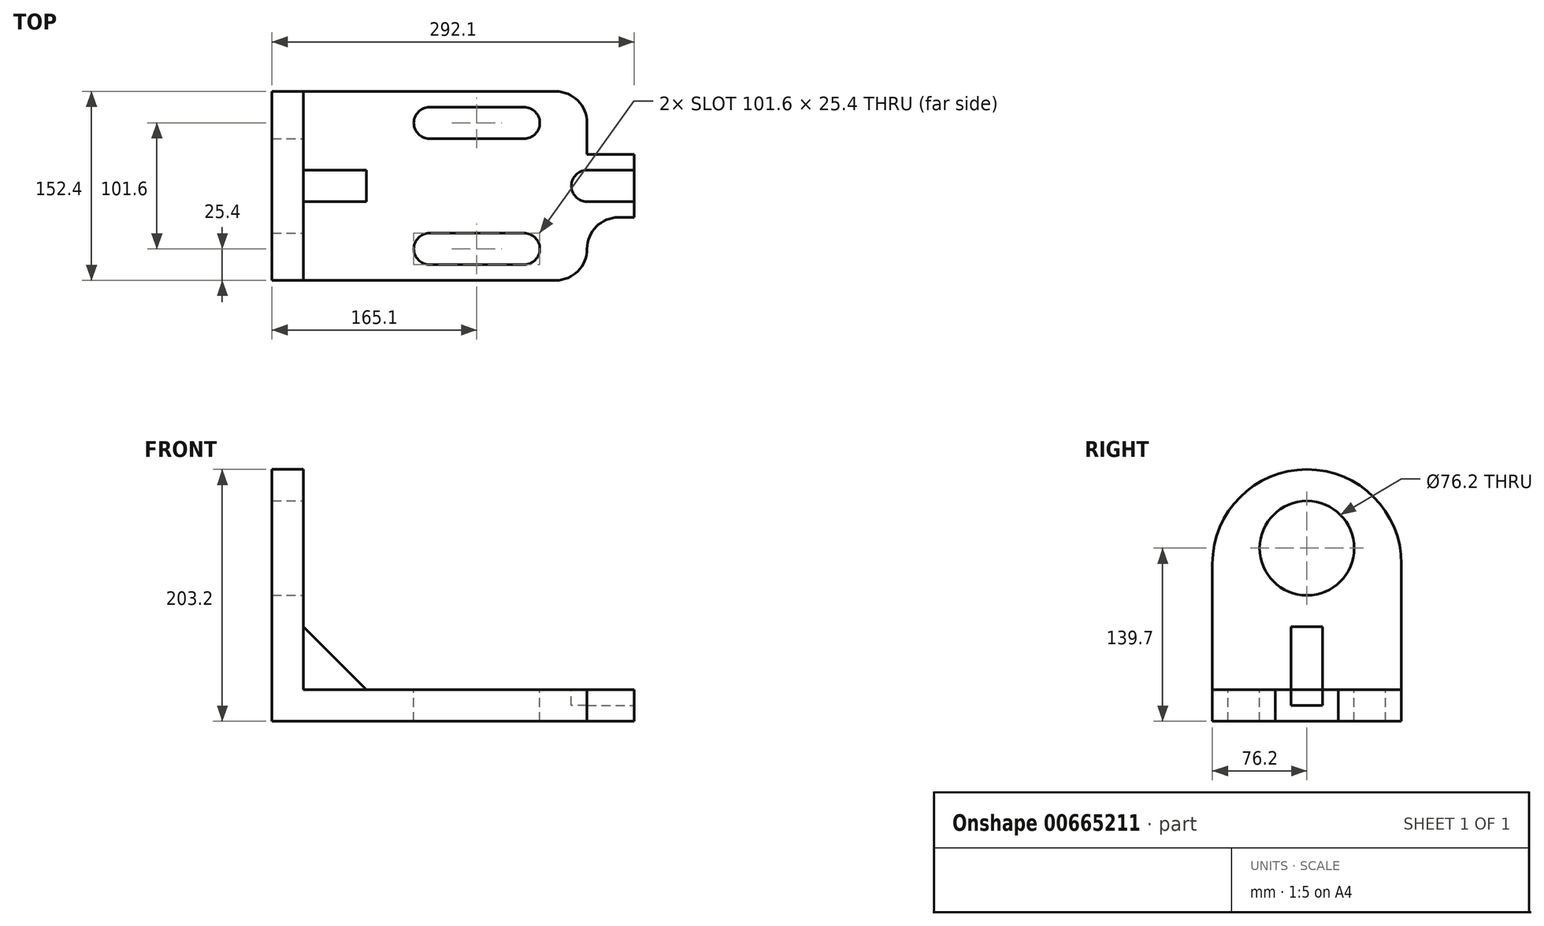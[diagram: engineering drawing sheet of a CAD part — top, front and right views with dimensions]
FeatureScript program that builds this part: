
annotation { "Feature Type Name" : "Feature", "Feature Type Description" : "" }
export const myFeature = defineFeature(function(context is Context, id is Id, definition is map)
    precondition{}
    {
        {
            var Q0;
            Q0=qCreatedBy(makeId("Front.planeOp"),FACE);
            var sketch = newSketch(context, id + "F0", { "sketchPlane" : qUnion([Q0])});
            skLineSegment(sketch, "E0", {"start": v(0, 0) * mm, "end": v(0, 203.2) * mm});
            skLineSegment(sketch, "E1", {"start": v(0, 203.2) * mm, "end": v(25.4, 203.2) * mm});
            skLineSegment(sketch, "E2", {"start": v(25.4, 203.2) * mm, "end": v(25.4, 25.4) * mm});
            skLineSegment(sketch, "E3", {"start": v(25.4, 25.4) * mm, "end": v(254, 25.4) * mm});
            skLineSegment(sketch, "E4", {"start": v(254, 25.4) * mm, "end": v(254, 0) * mm});
            skLineSegment(sketch, "E5", {"start": v(254, 0) * mm, "end": v(0, 0) * mm});
            skPoint(sketch, "E6", {"position": v(25.4, 114.3) * mm});
            skLineSegment(sketch, "E7", {"start": v(25.4, 76.2) * mm, "end": v(76.2, 25.4) * mm});
            skSolve(sketch);
        }
        {
            var Q0;
            Q0=makeQuery(id+"F0.imprint","IMPRINT",FACE,{"disambiguationData":[TD([[makeQuery(id+"F0.imprint","IMPRINT",EDGE,{"derivedFrom":sQuery(id+"F0.wireOp",EDGE,"E0")}),-1.0]])]});
            extrude(context, id + "F1", {"entities" : qUnion([Q0]), "endBound" : BoundingType.SYMMETRIC, "depth" : 152.4 * mm, "offsetDistance" : 25.4 * mm});
        }
        {
            var Q0;
            {var subQ3=sQuery(id+"F0.wireOp",EDGE,"nf9WDQkA-JbBY-tZqr-PVvL-w4dofeHm9VYt");Q0=makeQuery(id+"F0.imprint","IMPRINT",FACE,{"disambiguationData":[TD([[makeQuery(id+"F0.imprint","IMPRINT",EDGE,{"derivedFrom":subQ3}),-1.0]])]});}
            var Q1;
            {var subQ3=sQuery(id+"F0.wireOp",EDGE,"E7");Q1=makeQuery(id+"F0.imprint","IMPRINT",FACE,{"disambiguationData":[TD([[makeQuery(id+"F0.imprint","IMPRINT",EDGE,{"derivedFrom":subQ3}),-1.0]])]});}
            extrude(context, id + "F2", {"entities" : qUnion([Q0, Q1]), "operationType" : NewBodyOperationType.ADD, "endBound" : BoundingType.SYMMETRIC, "depth" : 25.4 * mm, "offsetDistance" : 25.4 * mm});
        }
        {
            var Q0;
            Q0=makeQuery(id+"F1.opExtrude","CAP_EDGE",EDGE,{"disambiguationData":[OSD([sQuery(id+"F0.wireOp",EDGE,"E1")])],"isStart":false});
            var Q1;
            Q1=makeQuery(id+"F1.opExtrude","CAP_EDGE",EDGE,{"disambiguationData":[OSD([sQuery(id+"F0.wireOp",EDGE,"E1")])],"isStart":true});
            fillet(context, id + "F3", {"entities" : qUnion([Q0, Q1]), "radius" : 76.2 * mm, "tangentPropagation" : true, "allowEdgeOverflow" : false});
        }
        {
            var Q0;
            Q0=makeQuery(id+"F1.opExtrude","SWEPT_FACE",FACE,{"disambiguationData":[OSD([sQuery(id+"F0.wireOp",EDGE,"E2")])]});
            var sketch = newSketch(context, id + "F4", { "sketchPlane" : qUnion([Q0])});
            skCircle(sketch, "E8", {"center": v(0, 139.7) * mm, "radius": 38.1 * mm});
            skPoint(sketch, "E8.centerSnap0", {"position": v(0, 203.2) * mm});
            skLineSegment(sketch, "E9", {"start": v(0, 203.2) * mm, "end": v(0, 76.2) * mm});
            skSolve(sketch);
        }
        {
            var Q0;
            Q0=makeQuery(id+"F1.opExtrude","SWEPT_FACE",FACE,{"disambiguationData":[OSD([sQuery(id+"F0.wireOp",EDGE,"E3")])]});
            var sketch = newSketch(context, id + "F5", { "sketchPlane" : qUnion([Q0])});
            skArc(sketch, "E10", {"start": v(127, -38.1) * mm, "mid": v(114.3, -50.8) * mm, "end": v(127, -63.5) * mm});
            skArc(sketch, "E11", {"start": v(203.2, -63.5) * mm, "mid": v(215.9, -50.8) * mm, "end": v(203.2, -38.1) * mm});
            skLineSegment(sketch, "E12", {"start": v(127, -63.5) * mm, "end": v(203.2, -63.5) * mm});
            skLineSegment(sketch, "E13", {"start": v(127, -38.1) * mm, "end": v(203.2, -38.1) * mm});
            skLineSegment(sketch, "E14.MirrorCS", {"start": v(127, 63.5) * mm, "end": v(203.2, 63.5) * mm});
            skArc(sketch, "E15.MirrorCS", {"start": v(203.2, 63.5) * mm, "mid": v(215.9, 50.8) * mm, "end": v(203.2, 38.1) * mm});
            skLineSegment(sketch, "E16.MirrorCS", {"start": v(127, 38.1) * mm, "end": v(203.2, 38.1) * mm});
            skArc(sketch, "E17.MirrorCS", {"start": v(127, 38.1) * mm, "mid": v(114.3, 50.8) * mm, "end": v(127, 63.5) * mm});
            skLineSegment(sketch, "E18", {"start": v(254, 25.4) * mm, "end": v(292.1, 25.4) * mm});
            skLineSegment(sketch, "E19", {"start": v(292.1, 25.4) * mm, "end": v(292.1, -25.4) * mm});
            skLineSegment(sketch, "E20", {"start": v(292.1, -25.4) * mm, "end": v(254, -25.4) * mm});
            skArc(sketch, "E21", {"start": v(254, 12.7) * mm, "mid": v(241.3, 0) * mm, "end": v(254, -12.7) * mm});
            skLineSegment(sketch, "E22", {"start": v(254, 12.7) * mm, "end": v(292.1, 12.7) * mm});
            skLineSegment(sketch, "E23", {"start": v(254, -12.7) * mm, "end": v(292.1, -12.7) * mm});
            skSolve(sketch);
        }
        {
            var Q0;
            Q0=makeQuery(id+"F5.imprint","IMPRINT",FACE,{"disambiguationData":[TD([[makeQuery(id+"F5.imprint","IMPRINT",EDGE,{"derivedFrom":sQuery(id+"F5.wireOp",EDGE,"E14.MirrorCS")}),-1.0]])]});
            var Q1;
            Q1=makeQuery(id+"F5.imprint","IMPRINT",FACE,{"disambiguationData":[TD([[makeQuery(id+"F5.imprint","IMPRINT",EDGE,{"derivedFrom":sQuery(id+"F5.wireOp",EDGE,"E10")}),1.0]])]});
            extrude(context, id + "F6", {"entities" : qUnion([Q0, Q1]), "operationType" : NewBodyOperationType.REMOVE, "endBound" : BoundingType.THROUGH_ALL, "oppositeDirection" : true, "depth" : 25.4 * mm, "offsetDistance" : 25.4 * mm});
        }
        {
            var Q0;
            Q0=makeQuery(id+"F4.imprint","IMPRINT",FACE,{"disambiguationData":[TD([[makeQuery(id+"F4.imprint","IMPRINT",EDGE,{"derivedFrom":sQuery(id+"F4.wireOp",EDGE,"E8")}),1.0]])]});
            extrude(context, id + "F7", {"entities" : qUnion([Q0]), "operationType" : NewBodyOperationType.REMOVE, "endBound" : BoundingType.THROUGH_ALL, "oppositeDirection" : true, "depth" : 25.4 * mm, "offsetDistance" : 25.4 * mm});
        }
        {
            var Q0;
            {var subQ0=sQuery(id+"F5.wireOp",EDGE,"E18");Q0=makeQuery(id+"F5.imprint","IMPRINT",FACE,{"disambiguationData":[TD([[makeQuery(id+"F5.imprint","IMPRINT",EDGE,{"derivedFrom":subQ0}),-1.0]])]});}
            var Q1;
            {var subQ0=sQuery(id+"F5.wireOp",EDGE,"E20");Q1=makeQuery(id+"F5.imprint","IMPRINT",FACE,{"disambiguationData":[TD([[makeQuery(id+"F5.imprint","IMPRINT",EDGE,{"derivedFrom":subQ0}),-1.0]])]});}
            var Q2;
            {var subQ0=sQuery(id+"F5.wireOp",EDGE,"E22");Q2=makeQuery(id+"F5.imprint","IMPRINT",FACE,{"disambiguationData":[TD([[makeQuery(id+"F5.imprint","IMPRINT",EDGE,{"derivedFrom":subQ0}),-1.0]])]});}
            extrude(context, id + "F8", {"entities" : qUnion([Q0, Q1, Q2]), "operationType" : NewBodyOperationType.ADD, "oppositeDirection" : true, "depth" : 25.4 * mm, "offsetDistance" : 25.4 * mm});
        }
        {
            var Q0;
            Q0=makeQuery(id+"F1.opExtrude","CAP_EDGE",EDGE,{"disambiguationData":[OSD([sQuery(id+"F0.wireOp",EDGE,"E4")])],"isStart":true});
            var Q1;
            Q1=makeQuery(id+"F1.opExtrude","CAP_EDGE",EDGE,{"disambiguationData":[OSD([sQuery(id+"F0.wireOp",EDGE,"E4")])],"isStart":false});
            fillet(context, id + "F9", {"entities" : qUnion([Q0, Q1]), "radius" : 25.4 * mm, "tangentPropagation" : true, "allowEdgeOverflow" : false});
        }
        {
            var Q0;
            Q0=makeQuery(id+"F8.opExtrude","SWEPT_EDGE",EDGE,{"disambiguationData":[OSD([sQuery(id+"F0.wireOp",EDGE,"E3"),sQuery(id+"F0.wireOp",EDGE,"E4"),sQuery(id+"F5.wireOp",EDGE,"E18")])]});
            var Q1;
            Q1=makeQuery(id+"F8.opExtrude","SWEPT_EDGE",EDGE,{"disambiguationData":[OSD([sQuery(id+"F0.wireOp",EDGE,"E3"),sQuery(id+"F0.wireOp",EDGE,"E4"),sQuery(id+"F5.wireOp",EDGE,"E20")])]});
            fillet(context, id + "F10", {"entities" : qUnion([Q0, Q1]), "radius" : 25.4 * mm, "tangentPropagation" : true, "allowEdgeOverflow" : false});
        }
        {
            var Q0;
            {var subQ0=sQuery(id+"F5.wireOp",EDGE,"E21");Q0=makeQuery(id+"F5.imprint","IMPRINT",FACE,{"disambiguationData":[TD([[makeQuery(id+"F5.imprint","IMPRINT",EDGE,{"derivedFrom":subQ0}),1.0]])]});}
            var Q1;
            {var subQ0=sQuery(id+"F5.wireOp",EDGE,"E22");Q1=makeQuery(id+"F5.imprint","IMPRINT",FACE,{"disambiguationData":[TD([[makeQuery(id+"F5.imprint","IMPRINT",EDGE,{"derivedFrom":subQ0}),-1.0]])]});}
            extrude(context, id + "F11", {"entities" : qUnion([Q0, Q1]), "operationType" : NewBodyOperationType.REMOVE, "oppositeDirection" : true, "depth" : 12.7 * mm, "offsetDistance" : 25.4 * mm});
        }
    });
